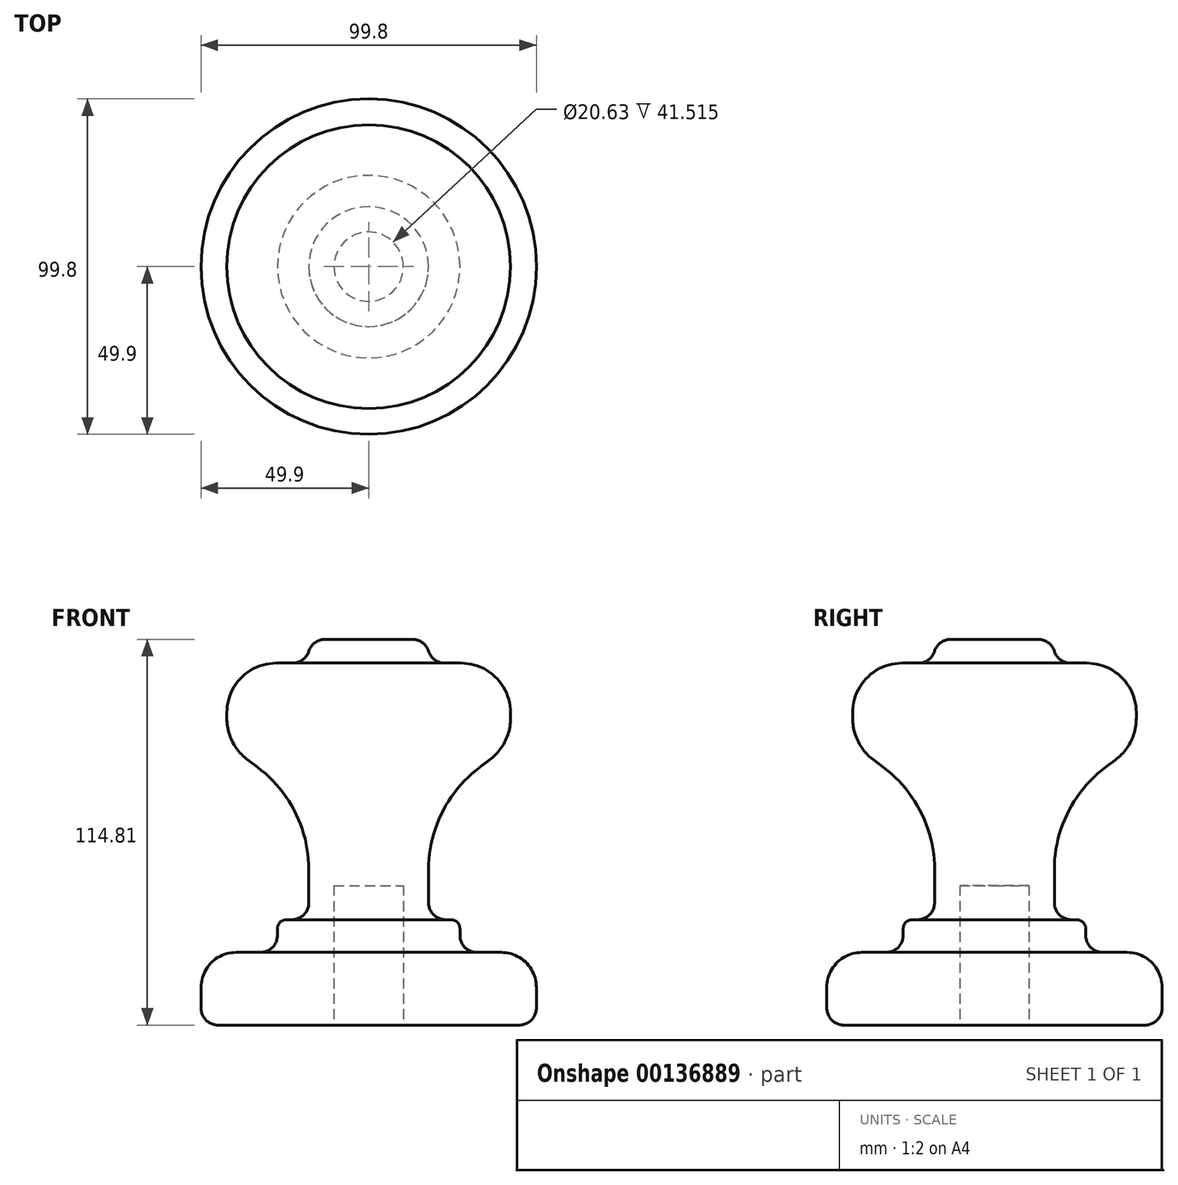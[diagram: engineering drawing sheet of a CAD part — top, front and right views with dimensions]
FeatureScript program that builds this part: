
annotation { "Feature Type Name" : "Feature", "Feature Type Description" : "" }
export const myFeature = defineFeature(function(context is Context, id is Id, definition is map)
    precondition{}
    {
        {
            var Q0;
            Q0=qCreatedBy(makeId("Front.planeOp"),FACE);
            var sketch = newSketch(context, id + "F0", { "sketchPlane" : qUnion([Q0])});
            skLineSegment(sketch, "E0", {"start": v(0, 0) * mm, "end": v(49.9, 0) * mm});
            skLineSegment(sketch, "E1", {"start": v(49.9, 21.63) * mm, "end": v(27.16, 21.63) * mm});
            skLineSegment(sketch, "E2", {"start": v(49.9, 21.63) * mm, "end": v(49.9, 0) * mm});
            skLineSegment(sketch, "E3", {"start": v(27.16, 21.63) * mm, "end": v(27.16, 31.35) * mm});
            skLineSegment(sketch, "E4", {"start": v(27.16, 31.35) * mm, "end": v(17.82, 31.35) * mm});
            skLineSegment(sketch, "E5", {"start": v(17.82, 31.35) * mm, "end": v(17.82, 65.34) * mm});
            skLineSegment(sketch, "E6", {"start": v(17.82, 65.34) * mm, "end": v(42.22, 83.56) * mm});
            skLineSegment(sketch, "E7", {"start": v(42.22, 83.56) * mm, "end": v(42.22, 107.71) * mm});
            skLineSegment(sketch, "E8", {"start": v(42.22, 107.71) * mm, "end": v(18.06, 107.71) * mm});
            skLineSegment(sketch, "E9", {"start": v(18.06, 107.71) * mm, "end": v(18.06, 114.8) * mm});
            skLineSegment(sketch, "E10", {"start": v(18.06, 114.8) * mm, "end": v(0, 114.8) * mm});
            skLineSegment(sketch, "E11", {"start": v(0, 0) * mm, "end": v(0, 154.04) * mm, "construction": true});
            skLineSegment(sketch, "E12", {"start": v(0, 114.8) * mm, "end": v(0, 0) * mm});
            skSolve(sketch);
        }
        {
            var Q0;
            {var subQ0=sQuery(id+"F0.wireOp",EDGE,"E2");Q0=makeQuery(id+"F0.imprint","IMPRINT",FACE,{"disambiguationData":[TD([[makeQuery(id+"F0.imprint","IMPRINT",EDGE,{"derivedFrom":subQ0}),1.0]])]});}
            var Q1;
            {var subQ0=sQuery(id+"F0.wireOp",EDGE,"E2");Q1=makeQuery(id+"F0.imprint","IMPRINT",FACE,{"disambiguationData":[TD([[makeQuery(id+"F0.imprint","IMPRINT",EDGE,{"derivedFrom":subQ0}),-1.0]])]});}
            var Q2;
            {var subQ0=sQuery(id+"F0.wireOp",EDGE,"E0");Q2=makeQuery(id+"F0.imprint","IMPRINT",FACE,{"disambiguationData":[TD([[makeQuery(id+"F0.imprint","IMPRINT",EDGE,{"derivedFrom":subQ0}),1.0]])]});}
            var Q3;
            Q3=sQuery(id+"F0.wireOp",EDGE,"E12");
            revolve(context, id + "F1", {"entities" : qUnion([Q0, Q1, Q2]), "axis" : qUnion([Q3]), "revolveType" : RevolveType.FULL});
        }
        {
            var Q0;
            Q0=makeQuery(id+"F1.opRevolve","SWEPT_EDGE",EDGE,{"disambiguationData":[OSD([sQuery(id+"F0.wireOp",EDGE,"E9"),sQuery(id+"F0.wireOp",EDGE,"E10")])]});
            fillet(context, id + "F2", {"entities" : qUnion([Q0]), "radius" : 5.08 * mm, "tangentPropagation" : true, "allowEdgeOverflow" : false});
        }
        {
            var Q0;
            Q0=makeQuery(id+"F1.opRevolve","SWEPT_EDGE",EDGE,{"disambiguationData":[OSD([sQuery(id+"F0.wireOp",EDGE,"E8"),sQuery(id+"F0.wireOp",EDGE,"E9")])]});
            fillet(context, id + "F3", {"entities" : qUnion([Q0]), "radius" : 5.08 * mm, "tangentPropagation" : true, "allowEdgeOverflow" : false});
        }
        {
            var Q0;
            Q0=makeQuery(id+"F1.opRevolve","SWEPT_EDGE",EDGE,{"disambiguationData":[OSD([sQuery(id+"F0.wireOp",EDGE,"E7"),sQuery(id+"F0.wireOp",EDGE,"E8")])]});
            fillet(context, id + "F4", {"entities" : qUnion([Q0]), "radius" : 14.73 * mm, "tangentPropagation" : true, "allowEdgeOverflow" : false});
        }
        {
            var Q0;
            Q0=makeQuery(id+"F1.opRevolve","SWEPT_EDGE",EDGE,{"disambiguationData":[OSD([sQuery(id+"F0.wireOp",EDGE,"E6"),sQuery(id+"F0.wireOp",EDGE,"E7")])]});
            fillet(context, id + "F5", {"entities" : qUnion([Q0]), "radius" : 15.5 * mm, "tangentPropagation" : true, "allowEdgeOverflow" : false});
        }
        {
            var Q0;
            Q0=makeQuery(id+"F1.opRevolve","SWEPT_EDGE",EDGE,{"disambiguationData":[OSD([sQuery(id+"F0.wireOp",EDGE,"E5"),sQuery(id+"F0.wireOp",EDGE,"E6")])]});
            fillet(context, id + "F6", {"entities" : qUnion([Q0]), "radius" : 38.1 * mm, "tangentPropagation" : true, "allowEdgeOverflow" : false});
        }
        {
            var Q0;
            Q0=makeQuery(id+"F1.opRevolve","SWEPT_EDGE",EDGE,{"disambiguationData":[OSD([sQuery(id+"F0.wireOp",EDGE,"E1"),sQuery(id+"F0.wireOp",EDGE,"E3")])]});
            fillet(context, id + "F7", {"entities" : qUnion([Q0]), "radius" : 5.08 * mm, "tangentPropagation" : true, "allowEdgeOverflow" : false});
        }
        {
            var Q0;
            Q0=makeQuery(id+"F1.opRevolve","SWEPT_EDGE",EDGE,{"disambiguationData":[OSD([sQuery(id+"F0.wireOp",EDGE,"E3"),sQuery(id+"F0.wireOp",EDGE,"E4")])]});
            fillet(context, id + "F8", {"entities" : qUnion([Q0]), "radius" : 2.65 * mm, "tangentPropagation" : true, "allowEdgeOverflow" : false});
        }
        {
            var Q0;
            Q0=makeQuery(id+"F1.opRevolve","SWEPT_EDGE",EDGE,{"disambiguationData":[OSD([sQuery(id+"F0.wireOp",EDGE,"E4"),sQuery(id+"F0.wireOp",EDGE,"E5")])]});
            fillet(context, id + "F9", {"entities" : qUnion([Q0]), "radius" : 5.08 * mm, "tangentPropagation" : true, "allowEdgeOverflow" : false});
        }
        {
            var Q0;
            Q0=makeQuery(id+"F1.opRevolve","SWEPT_EDGE",EDGE,{"disambiguationData":[OSD([sQuery(id+"F0.wireOp",EDGE,"E1"),sQuery(id+"F0.wireOp",EDGE,"E2")])]});
            fillet(context, id + "F10", {"entities" : qUnion([Q0]), "radius" : 10.4 * mm, "tangentPropagation" : true, "allowEdgeOverflow" : false});
        }
        {
            var Q0;
            Q0=makeQuery(id+"F1.opRevolve","SWEPT_EDGE",EDGE,{"disambiguationData":[OSD([sQuery(id+"F0.wireOp",EDGE,"E0"),sQuery(id+"F0.wireOp",EDGE,"E2")])]});
            fillet(context, id + "F11", {"entities" : qUnion([Q0]), "radius" : 5.08 * mm, "tangentPropagation" : true, "allowEdgeOverflow" : false});
        }
        {
            var Q0;
            Q0=makeQuery(id+"F1.opRevolve","SWEPT_FACE",FACE,{"disambiguationData":[OSD([sQuery(id+"F0.wireOp",EDGE,"E0")])]});
            var sketch = newSketch(context, id + "F12", { "sketchPlane" : qUnion([Q0])});
            skCircle(sketch, "E13", {"center": v(0, 0) * mm, "radius": 10.32 * mm});
            skSolve(sketch);
        }
        {
            var Q0;
            Q0=makeQuery(id+"F12.imprint","IMPRINT",FACE,{"disambiguationData":[TD([[makeQuery(id+"F12.imprint","IMPRINT",EDGE,{"derivedFrom":sQuery(id+"F12.wireOp",EDGE,"E13")}),1.0]])]});
            extrude(context, id + "F13", {"entities" : qUnion([Q0]), "operationType" : NewBodyOperationType.REMOVE, "oppositeDirection" : true, "depth" : 41.52 * mm});
        }
    });
